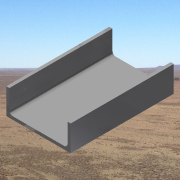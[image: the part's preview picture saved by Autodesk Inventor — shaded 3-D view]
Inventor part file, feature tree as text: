
AUTODESK INVENTOR PART (.ipt)
format: ipt  version: 2013 SP2 (Build 170200200, 200)  size: 123,904 bytes
history: native  units: in
note: dims shown in document units (in); Inventor stores cm internally (conversion verified against a paired STEP export)
features: extrude x1, sketch x1
ambient origin geometry x8: Origin, YZ Plane, XZ Plane, XY Plane, X Axis, Y Axis, Z Axis, Center Point
bodies: Solid1 (feature_tree)
feature tree (2):
  extrude  "Extrusion1"  Depth=1.0in
  sketch  "Sketch1"  dims[d0=2.5in d1=1.0in d2=0.12in d3=0.125in d4=4.0in d5=0.0in]
